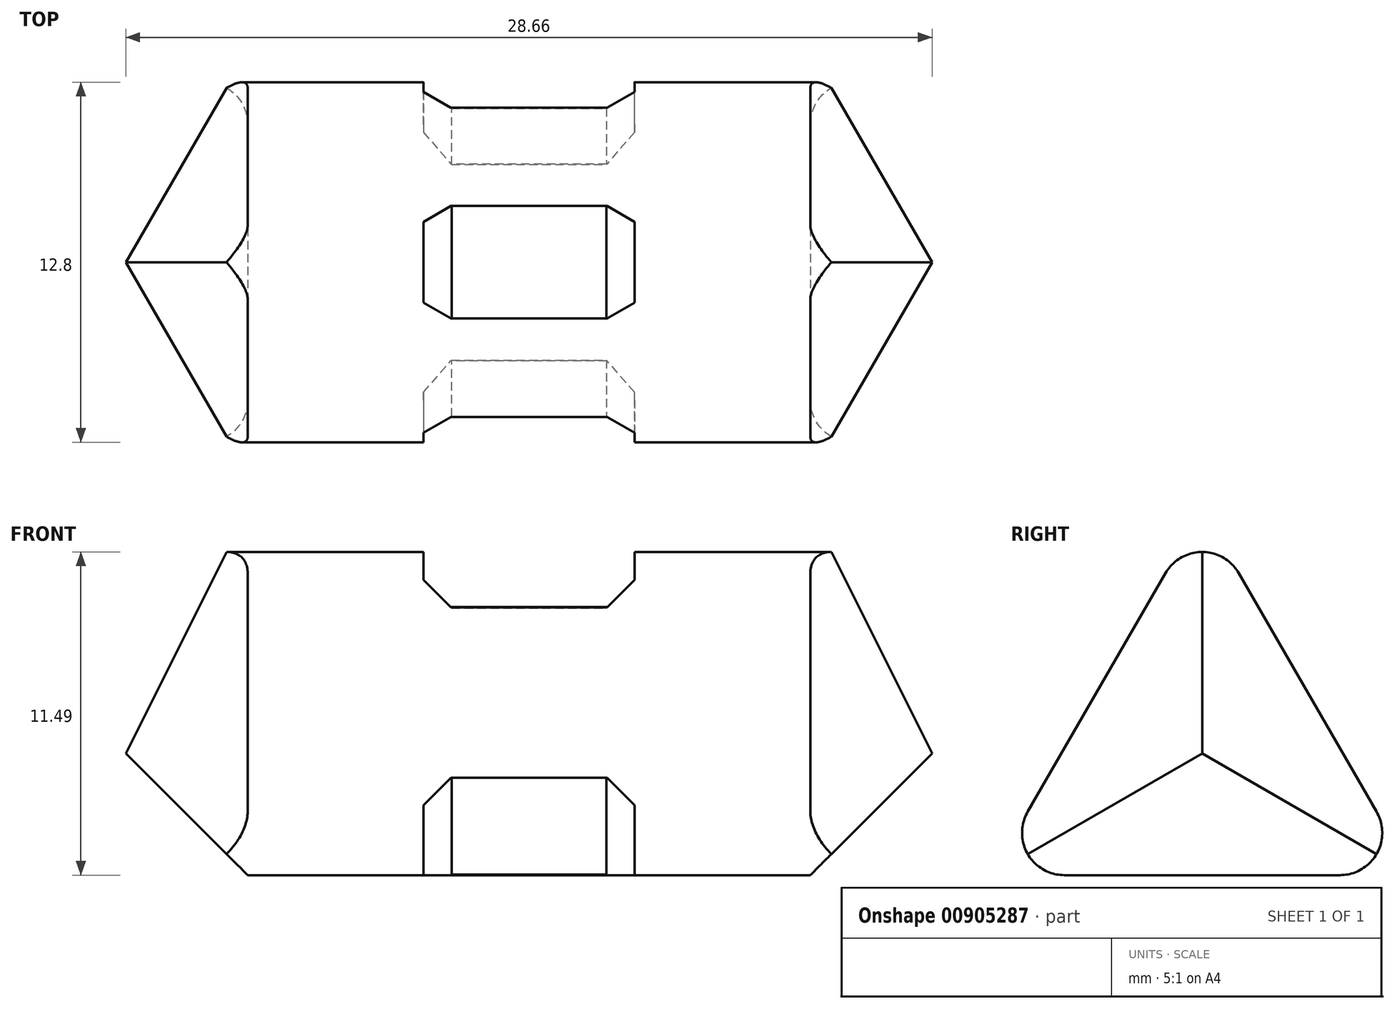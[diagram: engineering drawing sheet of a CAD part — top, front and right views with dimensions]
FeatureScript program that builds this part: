
annotation { "Feature Type Name" : "Feature", "Feature Type Description" : "" }
export const myFeature = defineFeature(function(context is Context, id is Id, definition is map)
    precondition{}
    {
        {
            var Q0;
            Q0=qCreatedBy(makeId("Right.planeOp"),FACE);
            var sketch = newSketch(context, id + "F0", { "sketchPlane" : qUnion([Q0])});
            skLineSegment(sketch, "E0", {"start": v(7.5, 0) * mm, "end": v(0, 13) * mm});
            skLineSegment(sketch, "E1", {"start": v(0, 13) * mm, "end": v(-7.5, 0) * mm});
            skLineSegment(sketch, "E2", {"start": v(7.5, 0) * mm, "end": v(-7.5, 0) * mm});
            skSolve(sketch);
        }
        {
            var Q0;
            Q0=makeQuery(id+"F0.imprint","IMPRINT",FACE,{"disambiguationData":[TD([[makeQuery(id+"F0.imprint","IMPRINT",EDGE,{"derivedFrom":sQuery(id+"F0.wireOp",EDGE,"E0")}),1.0]])]});
            extrude(context, id + "F1", {"entities" : qUnion([Q0]), "depth" : 20 * mm, "offsetDistance" : 25 * mm});
        }
        {
            var Q0;
            Q0=makeQuery(id+"F1.opExtrude","CAP_FACE",FACE,{"disambiguationData":[OSD([sQuery(id+"F0.wireOp",EDGE,"E0"),sQuery(id+"F0.wireOp",EDGE,"E1"),sQuery(id+"F0.wireOp",EDGE,"E2")])],"isStart":true});
            extrude(context, id + "F2", {"entities" : qUnion([Q0]), "operationType" : NewBodyOperationType.ADD, "depth" : 25 * mm, "offsetDistance" : 25 * mm, "hasDraft" : true, "draftAngle" : 45 * degree, "draftPullDirection" : true});
        }
        {
            var Q0;
            Q0=makeQuery(id+"F1.opExtrude","CAP_FACE",FACE,{"disambiguationData":[OSD([sQuery(id+"F0.wireOp",EDGE,"E0"),sQuery(id+"F0.wireOp",EDGE,"E1"),sQuery(id+"F0.wireOp",EDGE,"E2")])],"isStart":false});
            extrude(context, id + "F3", {"entities" : qUnion([Q0]), "operationType" : NewBodyOperationType.ADD, "depth" : 25 * mm, "offsetDistance" : 25 * mm, "hasDraft" : true, "draftAngle" : 45 * degree, "draftPullDirection" : true});
        }
        {
            var Q0;
            Q0=makeQuery(id+"F1.opExtrude","SWEPT_EDGE",EDGE,{"disambiguationData":[OSD([sQuery(id+"F0.wireOp",EDGE,"E0"),sQuery(id+"F0.wireOp",EDGE,"E1")])]});
            var Q1;
            Q1=makeQuery(id+"F1.opExtrude","SWEPT_EDGE",EDGE,{"disambiguationData":[OSD([sQuery(id+"F0.wireOp",EDGE,"E1"),sQuery(id+"F0.wireOp",EDGE,"E2")])]});
            var Q2;
            Q2=makeQuery(id+"F1.opExtrude","SWEPT_EDGE",EDGE,{"disambiguationData":[OSD([sQuery(id+"F0.wireOp",EDGE,"E0"),sQuery(id+"F0.wireOp",EDGE,"E2")])]});
            fillet(context, id + "F4", {"entities" : qUnion([Q0, Q1, Q2]), "radius" : 1.5 * mm, "tangentPropagation" : true, "allowEdgeOverflow" : false});
        }
        {
            var Q0;
            Q0=qCreatedBy(makeId("Top.planeOp"),FACE);
            var sketch = newSketch(context, id + "F5", { "sketchPlane" : qUnion([Q0])});
            skLineSegment(sketch, "E3.bottom", {"start": v(6.25, 2) * mm, "end": v(13.75, 2) * mm});
            skLineSegment(sketch, "E3.top", {"start": v(6.25, -2) * mm, "end": v(13.75, -2) * mm});
            skLineSegment(sketch, "E3.left", {"start": v(6.25, 2) * mm, "end": v(6.25, -2) * mm});
            skLineSegment(sketch, "E3.right", {"start": v(13.75, 2) * mm, "end": v(13.75, -2) * mm});
            skSolve(sketch);
        }
        {
            var Q0;
            Q0=makeQuery(id+"F5.imprint","IMPRINT",FACE,{"disambiguationData":[TD([[makeQuery(id+"F5.imprint","IMPRINT",EDGE,{"derivedFrom":sQuery(id+"F5.wireOp",EDGE,"E3.bottom")}),-1.0]])]});
            extrude(context, id + "F6", {"entities" : qUnion([Q0]), "operationType" : NewBodyOperationType.REMOVE, "depth" : 20 * mm, "offsetDistance" : 25 * mm, "hasSecondDirection" : true, "secondDirectionOppositeDirection" : false, "secondDirectionDepth" : 9.5 * mm});
        }
        {
            var Q0;
            Q0=makeQuery(id+"F1.opExtrude","SWEPT_FACE",FACE,{"disambiguationData":[OSD([sQuery(id+"F0.wireOp",EDGE,"E1")])]});
            var sketch = newSketch(context, id + "F7", { "sketchPlane" : qUnion([Q0])});
            skLineSegment(sketch, "E4.bottom", {"start": v(6.25, 1.75) * mm, "end": v(13.75, 1.75) * mm});
            skLineSegment(sketch, "E4.top", {"start": v(6.25, 5.75) * mm, "end": v(13.75, 5.75) * mm});
            skLineSegment(sketch, "E4.left", {"start": v(6.25, 1.75) * mm, "end": v(6.25, 5.75) * mm});
            skLineSegment(sketch, "E4.right", {"start": v(13.75, 1.75) * mm, "end": v(13.75, 5.75) * mm});
            skSolve(sketch);
        }
        {
            var Q0;
            Q0=makeQuery(id+"F7.imprint","IMPRINT",FACE,{"disambiguationData":[TD([[makeQuery(id+"F7.imprint","IMPRINT",EDGE,{"derivedFrom":sQuery(id+"F7.wireOp",EDGE,"E4.bottom")}),1.0]])]});
            extrude(context, id + "F8", {"entities" : qUnion([Q0]), "operationType" : NewBodyOperationType.REMOVE, "oppositeDirection" : true, "depth" : 25 * mm, "offsetDistance" : 25 * mm, "hasSecondDirection" : true, "secondDirectionOppositeDirection" : true, "secondDirectionDepth" : 9.5 * mm});
        }
        {
            var Q0;
            Q0=makeQuery(id+"F1.opExtrude","SWEPT_FACE",FACE,{"disambiguationData":[OSD([sQuery(id+"F0.wireOp",EDGE,"E0")])]});
            var sketch = newSketch(context, id + "F9", { "sketchPlane" : qUnion([Q0])});
            skLineSegment(sketch, "E5.bottom", {"start": v(-6.25, 1.75) * mm, "end": v(-13.75, 1.75) * mm});
            skLineSegment(sketch, "E5.top", {"start": v(-6.25, 5.75) * mm, "end": v(-13.75, 5.75) * mm});
            skLineSegment(sketch, "E5.left", {"start": v(-6.25, 1.75) * mm, "end": v(-6.25, 5.75) * mm});
            skLineSegment(sketch, "E5.right", {"start": v(-13.75, 1.75) * mm, "end": v(-13.75, 5.75) * mm});
            skSolve(sketch);
        }
        {
            var Q0;
            Q0=makeQuery(id+"F9.imprint","IMPRINT",FACE,{"disambiguationData":[TD([[makeQuery(id+"F9.imprint","IMPRINT",EDGE,{"derivedFrom":sQuery(id+"F9.wireOp",EDGE,"E5.bottom")}),-1.0]])]});
            extrude(context, id + "F10", {"entities" : qUnion([Q0]), "operationType" : NewBodyOperationType.REMOVE, "oppositeDirection" : true, "depth" : 20 * mm, "offsetDistance" : 25 * mm, "hasSecondDirection" : true, "secondDirectionOppositeDirection" : true, "secondDirectionDepth" : 9.5 * mm});
        }
        {
            var Q0;
            Q0=makeQuery(id+"F8.boolean.opBoolean","COPY",EDGE,{"derivedFrom":makeQuery(id+"F8.opExtrude","CAP_EDGE",EDGE,{"disambiguationData":[OSD([sQuery(id+"F7.wireOp",EDGE,"E4.left")])],"isStart":true})});
            var Q1;
            Q1=makeQuery(id+"F8.boolean.opBoolean","COPY",EDGE,{"derivedFrom":makeQuery(id+"F8.opExtrude","CAP_EDGE",EDGE,{"disambiguationData":[OSD([sQuery(id+"F7.wireOp",EDGE,"E4.right")])],"isStart":true})});
            var Q2;
            Q2=makeQuery(id+"F10.boolean.opBoolean","COPY",EDGE,{"derivedFrom":makeQuery(id+"F10.opExtrude","CAP_EDGE",EDGE,{"disambiguationData":[OSD([sQuery(id+"F9.wireOp",EDGE,"E5.left")])],"isStart":true})});
            var Q3;
            Q3=makeQuery(id+"F10.boolean.opBoolean","COPY",EDGE,{"derivedFrom":makeQuery(id+"F10.opExtrude","CAP_EDGE",EDGE,{"disambiguationData":[OSD([sQuery(id+"F9.wireOp",EDGE,"E5.right")])],"isStart":true})});
            var Q4;
            Q4=makeQuery(id+"F6.boolean.opBoolean","COPY",EDGE,{"derivedFrom":makeQuery(id+"F6.opExtrude","CAP_EDGE",EDGE,{"disambiguationData":[OSD([sQuery(id+"F5.wireOp",EDGE,"E3.left")])],"isStart":true})});
            var Q5;
            Q5=makeQuery(id+"F6.boolean.opBoolean","COPY",EDGE,{"derivedFrom":makeQuery(id+"F6.opExtrude","CAP_EDGE",EDGE,{"disambiguationData":[OSD([sQuery(id+"F5.wireOp",EDGE,"E3.right")])],"isStart":true})});
            chamfer(context, id + "F11", {"entities" : qUnion([Q0, Q1, Q2, Q3, Q4, Q5]), "width" : 1 * mm, "tangentPropagation" : true});
        }
    });
